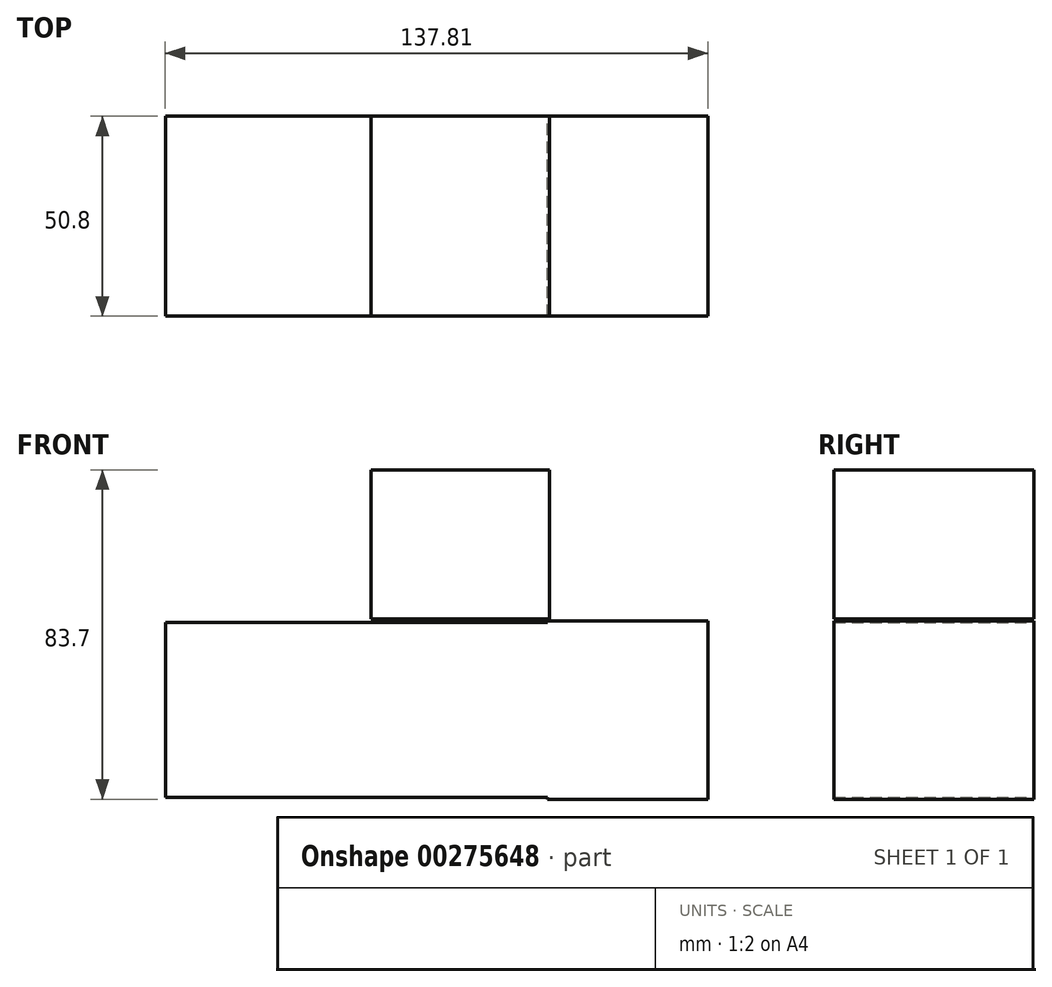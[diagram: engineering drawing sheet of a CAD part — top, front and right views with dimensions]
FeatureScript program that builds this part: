
annotation { "Feature Type Name" : "Feature", "Feature Type Description" : "" }
export const myFeature = defineFeature(function(context is Context, id is Id, definition is map)
    precondition{}
    {
        {
            var Q0;
            Q0=qCreatedBy(makeId("Front.planeOp"),FACE);
            var sketch = newSketch(context, id + "F0", { "sketchPlane" : qUnion([Q0])});
            skLineSegment(sketch, "E0.bottom", {"start": v(22.66, 0) * mm, "end": v(-22.66, 0) * mm});
            skLineSegment(sketch, "E0.top", {"start": v(22.66, 37.92) * mm, "end": v(-22.66, 37.92) * mm});
            skLineSegment(sketch, "E0.left", {"start": v(22.66, 0) * mm, "end": v(22.66, 37.92) * mm});
            skLineSegment(sketch, "E0.right", {"start": v(-22.66, 0) * mm, "end": v(-22.66, 37.92) * mm});
            skPoint(sketch, "E0.middle", {"position": v(0, 18.96) * mm});
            skLineSegment(sketch, "E1.bottom", {"start": v(22.2, -45.32) * mm, "end": v(-22.2, -45.32) * mm});
            skLineSegment(sketch, "E1.top", {"start": v(22.2, -0.92) * mm, "end": v(-22.2, -0.92) * mm});
            skLineSegment(sketch, "E1.left", {"start": v(22.2, -45.32) * mm, "end": v(22.2, -0.92) * mm});
            skLineSegment(sketch, "E1.right", {"start": v(-22.2, -45.32) * mm, "end": v(-22.2, -0.92) * mm});
            skPoint(sketch, "E1.middle", {"position": v(0, -23.12) * mm});
            skLineSegment(sketch, "E2.bottom", {"start": v(62.9, -45.78) * mm, "end": v(22.2, -45.78) * mm});
            skLineSegment(sketch, "E2.top", {"start": v(62.9, -0.46) * mm, "end": v(22.2, -0.46) * mm});
            skLineSegment(sketch, "E2.left", {"start": v(62.9, -45.78) * mm, "end": v(62.9, -0.46) * mm});
            skLineSegment(sketch, "E2.right", {"start": v(22.2, -45.78) * mm, "end": v(22.2, -0.46) * mm});
            skPoint(sketch, "E2.middle", {"position": v(42.55, -23.12) * mm});
            skLineSegment(sketch, "E3.bottom", {"start": v(-22.2, -45.32) * mm, "end": v(-74.92, -45.32) * mm});
            skLineSegment(sketch, "E3.top", {"start": v(-22.2, -0.92) * mm, "end": v(-74.92, -0.92) * mm});
            skLineSegment(sketch, "E3.right", {"start": v(-74.92, -45.32) * mm, "end": v(-74.92, -0.92) * mm});
            skPoint(sketch, "E3.middle", {"position": v(-48.56, -23.12) * mm});
            skSolve(sketch);
        }
        {
            var Q0;
            {var subQ2=sQuery(id+"F0.wireOp",EDGE,"E2.bottom");Q0=makeQuery(id+"F0.imprint","IMPRINT",FACE,{"disambiguationData":[TD([[makeQuery(id+"F0.imprint","IMPRINT",EDGE,{"derivedFrom":subQ2}),-1.0]])]});}
            var Q1;
            {var subQ0=sQuery(id+"F0.wireOp",EDGE,"E1.bottom");Q1=makeQuery(id+"F0.imprint","IMPRINT",FACE,{"disambiguationData":[TD([[makeQuery(id+"F0.imprint","IMPRINT",EDGE,{"derivedFrom":subQ0}),-1.0]])]});}
            var Q2;
            Q2=makeQuery(id+"F0.imprint","IMPRINT",FACE,{"disambiguationData":[TD([[makeQuery(id+"F0.imprint","IMPRINT",EDGE,{"derivedFrom":sQuery(id+"F0.wireOp",EDGE,"E3.bottom")}),-1.0]])]});
            var Q3;
            Q3=makeQuery(id+"F0.imprint","IMPRINT",FACE,{"disambiguationData":[TD([[makeQuery(id+"F0.imprint","IMPRINT",EDGE,{"derivedFrom":sQuery(id+"F0.wireOp",EDGE,"E0.bottom")}),-1.0]])]});
            extrude(context, id + "F1", {"entities" : qUnion([Q0, Q1, Q2, Q3]), "depth" : 50.8 * mm});
        }
    });
